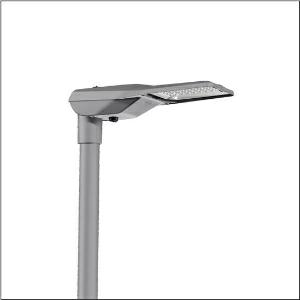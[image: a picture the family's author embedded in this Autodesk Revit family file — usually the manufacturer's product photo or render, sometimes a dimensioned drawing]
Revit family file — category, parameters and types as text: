
# Revit family: streetlight_sl_21_iq_mini___st1_0a_5xe2d61y08jb_b42a
name_source: partatom
category: Lighting Fixtures
units: mm (PartAtom-declared; Revit-internal decimal feet)

## family parameters
Cut with Voids When Loaded = No
Host = Face
Light Source = No
Part Type = Normal
Room Calculation Point = No
Round Connector Dimension = Use Diameter
Shared = No

## types (1)
- --- (1 x LED, 9730 lm, 72.5 W, 2700K)
    Apparent Load = 73 VA
    CIE Flux Codes = 40 73 97 100 100
    Color Rendering = 70
    Color Temperature = 2700K
    Default Elevation = 1800 mm
    Description = Streetlight SL 21 iQ mini, mast luminaire, primary light control with lens, of PMMA, primary optical cover: cover, of toughened safety glass, transparent, light distribution: ST1.0a, light emission: direct distribution, primary light characteristic: asymmetric, installation type: post-top, side-entry, LED, High Power LED, rated luminous flux: 9.730lm, luminous efficacy: 134lm/W, light colour: 727, colour temperature: 2700K, control: presetting dimming logarithmic, Street-Remote, Auto-Match, Temp-Guard, Lumen-Switch, Night-Set, Smart-Wire, Light-Fading, Desk-Remote (wireless, voltage-free reading and setting of iQ features in the workshop via application-optimized NFC function/RFID function), optimised constant luminous flux control (CLO 2.0), mains connection: 220..240V, AC, 50/60Hz, start of lifetime: 73W, end of service life: 76W, reduction: 33W, luminaire housing, of diecast aluminium, powder-coated, Siteco® metallic grey (DB 702S), corrosivity category C5 mid according to DIN EN ISO 12944, please order mast flange separately, inclination adjustable: 0°, 5°, 10°, 15°, sealing non-destructively replaceable, multi-level sealing system, length: 628mm, width: 235mm, height: 110mm, mast flange for spigot size: 42mm (side-entry): 5XC10008XM4, 60/48mm (side-entry/post-top): 5XC10108XM2, 76/60mm (side-entry/post-top): 5XC10108XM1, Smart Interface below and above, protection rating (complete): IP66, insulation class (complete): insulation class II (safety insulation), certification: CE, ENEC, ENEC+, VDE, impact resistance: IK09, permissible operating ambient temperature for outdoor applications: -40..+50°C, standard-compliant lighting for roads and squares, packaging unit: 1 piece

Light Distribution: ST1.0a
    Height = 110 mm
    Lamp = 1 x LED
    Lamp Light Flux = 9730 lm
    Lamp Power = 72.5 W
    Lamp count = 1
    Length = 625 mm
    Luminous efficacy = 134 lm/W
    Manufacturer = Siteco
    ModVariant = No
    Model = 5XE2D61Y08JB
    Number of Poles = 1
    OnlyDefault = Yes
    Power Factor = 1
    Product Name = Streetlight SL 21 iQ mini | ST1.0a
    Product group = mast luminaire | pylon top
    ProductGroupID = 6100
    Protection Class = Protection class II
    Protection Degree = IP 66
    RLX_Detail_Level = 1
    RLX_Emergency_Light_Flux = 0 lm
    RLX_Emergency_Type = 0
    RLX_Emergency_Type_DB = No
    RlxData = <blob elided: 92689 chars, md5=14c5ba7b>
    Socket = socket
    Standby Power = 0 W
    System Light Flux = 9730 lm
    System Power = 73 W
    Type Comments = factory setting: luminous flux: 100 % | dim-lin: 254 | 755 mA
    Type Image = l_1003514.jpg
    URL = http://relux.com
    VarID = @adj_062307
    Voltage = 0 V
    Weight = 0.00 kg
    Width = 234 mm

## geometry (parser evidence)
native form markers: Blend x4, Sweep x10
no freeform markers — native parametric forms only
